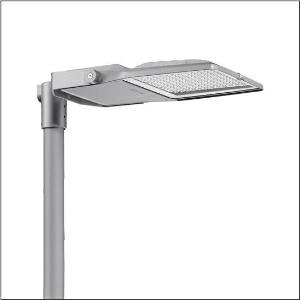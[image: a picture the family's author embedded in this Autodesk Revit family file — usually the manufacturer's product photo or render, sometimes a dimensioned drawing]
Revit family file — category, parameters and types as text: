
# Revit family: floodlight_fl_21_iq_midi___pl61_5xa7781f2c3a_20a4
name_source: partatom
category: Lighting Fixtures
units: mm (PartAtom-declared; Revit-internal decimal feet)

## family parameters
Cut with Voids When Loaded = No
Host = Face
Light Source = No
Part Type = Normal
Room Calculation Point = No
Round Connector Dimension = Use Diameter
Shared = No

## types (1)
- --- (1 x LED, 35100 lm, 270.2 W, 3000K)
    Apparent Load = 270 VA
    CIE Flux Codes = 33 65 98 100 100
    Color Rendering = 70
    Color Temperature = 3000K
    Default Elevation = 1800 mm
    Description = Floodlight FL 21 iQ midi, floodlight, primary light control with lens, of PMMA, primary optical cover: protective disc, of toughened safety glass, transparent, light distribution: PL61, light emission: direct distribution, installation type: surface-mounted, LED, High Power LED, rated luminous flux: 35.100lm, luminous efficacy: 130lm/W, light colour: 730, colour temperature: 3000K, control gear: ECG iQ, control: optimised constant luminous flux control (CLO 2.0), Desk-Remote (wireless, voltage-free reading and setting of iQ features in the workshop via application-optimized NFC function/RFID function), Light-Fading, Smart-Wire, Night-Set, Lumen-Switch, Temp-Guard, Auto-Match, with terminal, 6-pole, mains connection: 220..240V, AC, 50/60Hz, start of lifetime: 270W, end of service life: 287W, reduction: 117W, luminaire housing, of diecast aluminium, powder-coated, Siteco® metallic grey (DB 702S), corrosivity category C5 mid according to DIN EN ISO 12944, sealing non-destructively replaceable, please order mast flange separately, mast bracket, of steel, galvanised, powder-coated, Siteco® metallic grey (DB 702S), protection rating (complete): IP66, insulation class (complete): insulation class II (safety insulation), certification: CE, protection symbol: D, impact resistance: IK08, permissible operating ambient temperature: -40..+40°C, permissible operating ambient temperature for outdoor applications: -40..+50°C, standard: DIN EN 12944, LABS conformity tested according to VDMA 24364:2018-05, packaging unit: 1 piece

Light Distribution: PL61
    Height = 76 mm
    Lamp = 1 x LED
    Lamp Light Flux = 35100 lm
    Lamp Power = 270.2 W
    Lamp count = 1
    Length = 657 mm
    Luminous efficacy = 130 lm/W
    Manufacturer = Siteco
    ModVariant = No
    Model = 5XA7781F2C3A
    Number of Poles = 1
    OnlyDefault = Yes
    Power Factor = 1
    Product Name = Floodlight FL 21 iQ midi | PL61
    Product group = floodlight | pylon annexe
    ProductGroupID = 6200
    Protection Class = Protection class II
    Protection Degree = IP 66
    RLX_Detail_Level = 1
    RLX_Emergency_Light_Flux = 0 lm
    RLX_Emergency_Type = 0
    RLX_Emergency_Type_DB = No
    RlxData = <blob elided: 153881 chars, md5=fc35acdc>
    Socket = socket
    Standby Power = 0 W
    System Light Flux = 35100 lm
    System Power = 270 W
    Type Comments = factory setting: luminous flux: 100 % | dim-lin: 254 | 620 mA
    Type Image = l_1007123.jpg
    URL = http://relux.com
    VarID = @adj_056773
    Voltage = 0 V
    Weight = 0.00 kg
    Width = 442 mm

## geometry (parser evidence)
native form markers: Blend x4, Sweep x12
no freeform markers — native parametric forms only
